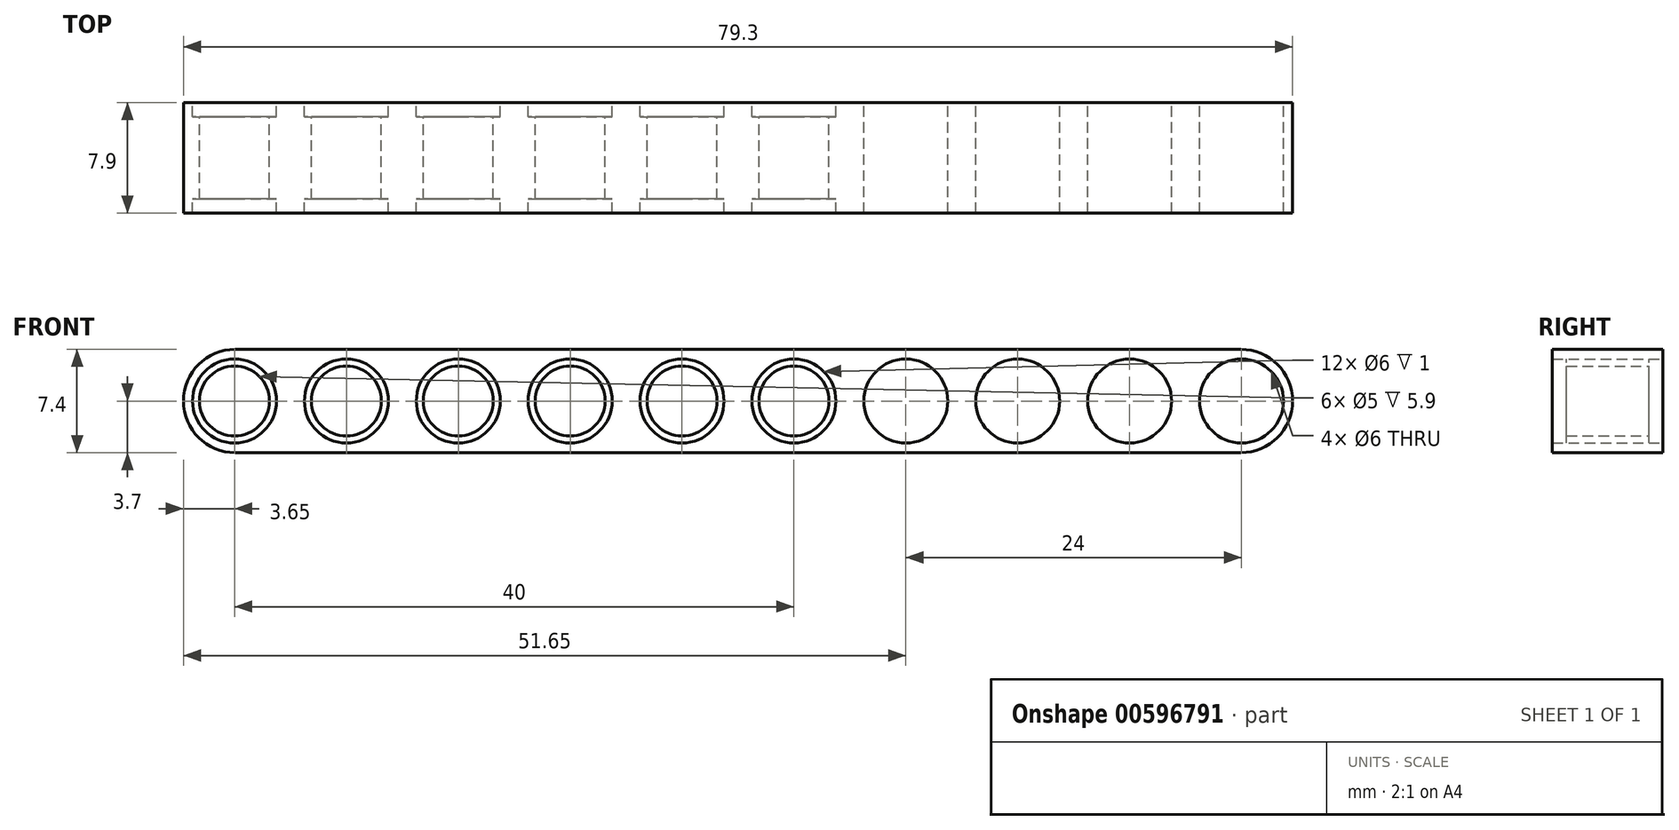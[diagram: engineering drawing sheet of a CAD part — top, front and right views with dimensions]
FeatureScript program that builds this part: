
annotation { "Feature Type Name" : "Feature", "Feature Type Description" : "" }
export const myFeature = defineFeature(function(context is Context, id is Id, definition is map)
    precondition{}
    {
        {
            var Q0;
            Q0=qCreatedBy(makeId("Front.planeOp"),FACE);
            var sketch = newSketch(context, id + "F0", { "sketchPlane" : qUnion([Q0])});
            skLineSegment(sketch, "E0.bottom", {"start": v(35.65, 3.7) * mm, "end": v(-43.65, 3.7) * mm});
            skLineSegment(sketch, "E0.top", {"start": v(35.65, -3.7) * mm, "end": v(-43.65, -3.7) * mm});
            skLineSegment(sketch, "E0.right", {"start": v(-43.65, 3.7) * mm, "end": v(-43.65, -3.7) * mm});
            skPoint(sketch, "E0.middle", {"position": v(0, 0) * mm});
            skCircle(sketch, "E1", {"center": v(0, 0) * mm, "radius": 3 * mm});
            skCircle(sketch, "E2", {"center": v(-8, 0) * mm, "radius": 3 * mm});
            skCircle(sketch, "E3", {"center": v(-16, 0) * mm, "radius": 3 * mm});
            skCircle(sketch, "E4", {"center": v(-24, 0) * mm, "radius": 3 * mm});
            skCircle(sketch, "E5", {"center": v(-32, 0) * mm, "radius": 3 * mm});
            skCircle(sketch, "E6", {"center": v(-40, 0) * mm, "radius": 3 * mm});
            skLineSegment(sketch, "E7", {"start": v(0, 12.95) * mm, "end": v(0, -12.5) * mm, "construction": true});
            skPoint(sketch, "E7.endSnap0", {"position": v(0, -3.7) * mm});
            skCircle(sketch, "E8.MirrorC", {"center": v(8, 0) * mm, "radius": 3 * mm});
            skCircle(sketch, "E9.MirrorC", {"center": v(16, 0) * mm, "radius": 3 * mm});
            skCircle(sketch, "E10.MirrorC", {"center": v(24, 0) * mm, "radius": 3 * mm});
            skCircle(sketch, "E11.MirrorC", {"center": v(32, 0) * mm, "radius": 3 * mm});
            skLineSegment(sketch, "E12", {"start": v(35.65, 3.7) * mm, "end": v(35.65, -3.7) * mm});
            skCircle(sketch, "E13", {"center": v(0, 0) * mm, "radius": 2.5 * mm});
            skCircle(sketch, "E14", {"center": v(-8, 0) * mm, "radius": 2.5 * mm});
            skCircle(sketch, "E15", {"center": v(-16, 0) * mm, "radius": 2.5 * mm});
            skCircle(sketch, "E16", {"center": v(-24, 0) * mm, "radius": 2.5 * mm});
            skCircle(sketch, "E17", {"center": v(-32, 0) * mm, "radius": 2.5 * mm});
            skCircle(sketch, "E18", {"center": v(-40, 0) * mm, "radius": 2.5 * mm});
            skCircle(sketch, "E19.MirrorC", {"center": v(8, 0) * mm, "radius": 2.5 * mm});
            skCircle(sketch, "E20.MirrorC", {"center": v(16, 0) * mm, "radius": 2.5 * mm});
            skCircle(sketch, "E21.MirrorC", {"center": v(24, 0) * mm, "radius": 2.5 * mm});
            skCircle(sketch, "E22.MirrorC", {"center": v(32, 0) * mm, "radius": 2.5 * mm});
            skSolve(sketch);
        }
        {
            var Q0;
            Q0=qSketchRegion(id+"F0",true);
            extrude(context, id + "F1", {"entities" : qUnion([Q0]), "endBound" : BoundingType.SYMMETRIC, "depth" : 7.9 * mm, "offsetDistance" : 25 * mm});
        }
        {
            var Q0;
            Q0=makeQuery(id+"F0.imprint","IMPRINT",FACE,{"disambiguationData":[TD([[makeQuery(id+"F0.imprint","IMPRINT",EDGE,{"derivedFrom":sQuery(id+"F0.wireOp",EDGE,"E6")}),1.0]])]});
            var Q1;
            Q1=makeQuery(id+"F0.imprint","IMPRINT",FACE,{"disambiguationData":[TD([[makeQuery(id+"F0.imprint","IMPRINT",EDGE,{"derivedFrom":sQuery(id+"F0.wireOp",EDGE,"E5")}),1.0]])]});
            var Q2;
            Q2=makeQuery(id+"F0.imprint","IMPRINT",FACE,{"disambiguationData":[TD([[makeQuery(id+"F0.imprint","IMPRINT",EDGE,{"derivedFrom":sQuery(id+"F0.wireOp",EDGE,"E4")}),1.0]])]});
            var Q3;
            Q3=makeQuery(id+"F0.imprint","IMPRINT",FACE,{"disambiguationData":[TD([[makeQuery(id+"F0.imprint","IMPRINT",EDGE,{"derivedFrom":sQuery(id+"F0.wireOp",EDGE,"E3")}),1.0]])]});
            var Q4;
            Q4=makeQuery(id+"F0.imprint","IMPRINT",FACE,{"disambiguationData":[TD([[makeQuery(id+"F0.imprint","IMPRINT",EDGE,{"derivedFrom":sQuery(id+"F0.wireOp",EDGE,"E2")}),1.0]])]});
            var Q5;
            Q5=makeQuery(id+"F0.imprint","IMPRINT",FACE,{"disambiguationData":[TD([[makeQuery(id+"F0.imprint","IMPRINT",EDGE,{"derivedFrom":sQuery(id+"F0.wireOp",EDGE,"E1")}),1.0]])]});
            var Q6;
            Q6=makeQuery(id+"F0.imprint","IMPRINT",FACE,{"disambiguationData":[TD([[makeQuery(id+"F0.imprint","IMPRINT",EDGE,{"derivedFrom":sQuery(id+"F0.wireOp",EDGE,"E8.MirrorC")}),-1.0]])]});
            var Q7;
            Q7=makeQuery(id+"F0.imprint","IMPRINT",FACE,{"disambiguationData":[TD([[makeQuery(id+"F0.imprint","IMPRINT",EDGE,{"derivedFrom":sQuery(id+"F0.wireOp",EDGE,"E9.MirrorC")}),-1.0]])]});
            var Q8;
            Q8=makeQuery(id+"F0.imprint","IMPRINT",FACE,{"disambiguationData":[TD([[makeQuery(id+"F0.imprint","IMPRINT",EDGE,{"derivedFrom":sQuery(id+"F0.wireOp",EDGE,"E10.MirrorC")}),-1.0]])]});
            var Q9;
            Q9=makeQuery(id+"F0.imprint","IMPRINT",FACE,{"disambiguationData":[TD([[makeQuery(id+"F0.imprint","IMPRINT",EDGE,{"derivedFrom":sQuery(id+"F0.wireOp",EDGE,"E11.MirrorC")}),-1.0]])]});
            extrude(context, id + "F2", {"entities" : qUnion([Q0, Q1, Q2, Q3, Q4, Q5, Q6, Q7, Q8, Q9]), "operationType" : NewBodyOperationType.ADD, "endBound" : BoundingType.SYMMETRIC, "depth" : 5.9 * mm, "offsetDistance" : 25 * mm});
        }
        {
            var Q0;
            Q0=makeQuery(id+"F1.opExtrude","SWEPT_EDGE",EDGE,{"disambiguationData":[OSD([sQuery(id+"F0.wireOp",EDGE,"E0.bottom"),sQuery(id+"F0.wireOp",EDGE,"E0.right")])]});
            var Q1;
            Q1=makeQuery(id+"F1.opExtrude","SWEPT_EDGE",EDGE,{"disambiguationData":[OSD([sQuery(id+"F0.wireOp",EDGE,"E0.bottom"),sQuery(id+"F0.wireOp",EDGE,"E12")])]});
            var Q2;
            Q2=makeQuery(id+"F1.opExtrude","SWEPT_EDGE",EDGE,{"disambiguationData":[OSD([sQuery(id+"F0.wireOp",EDGE,"E0.top"),sQuery(id+"F0.wireOp",EDGE,"E12")])]});
            var Q3;
            Q3=makeQuery(id+"F1.opExtrude","SWEPT_EDGE",EDGE,{"disambiguationData":[OSD([sQuery(id+"F0.wireOp",EDGE,"E0.top"),sQuery(id+"F0.wireOp",EDGE,"E0.right")])]});
            fillet(context, id + "F3", {"entities" : qUnion([Q0, Q1, Q2, Q3]), "radius" : 3.7 * mm, "tangentPropagation" : true, "allowEdgeOverflow" : false});
        }
    });
